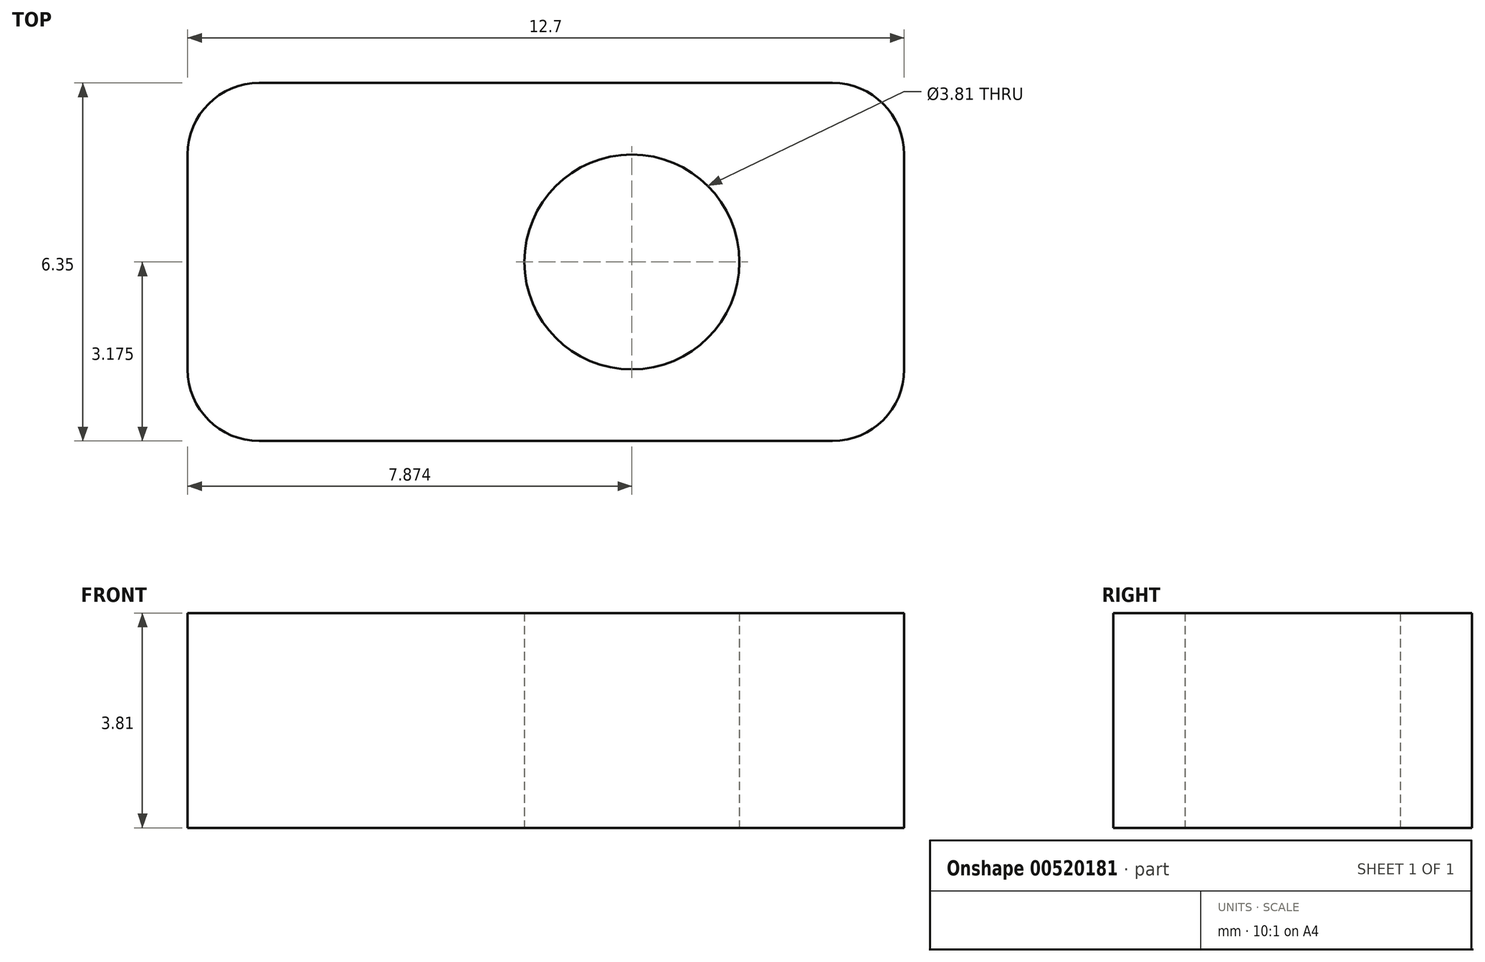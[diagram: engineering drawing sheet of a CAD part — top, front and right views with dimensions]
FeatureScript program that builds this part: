
annotation { "Feature Type Name" : "Feature", "Feature Type Description" : "" }
export const myFeature = defineFeature(function(context is Context, id is Id, definition is map)
    precondition{}
    {
        {
            var Q0;
            Q0=qCreatedBy(makeId("Top.planeOp"),FACE);
            var sketch = newSketch(context, id + "F0", { "sketchPlane" : qUnion([Q0])});
            skLineSegment(sketch, "E0.bottom", {"start": v(0, 0) * mm, "end": v(-12.7, 0) * mm});
            skLineSegment(sketch, "E0.top", {"start": v(0, 6.35) * mm, "end": v(-12.7, 6.35) * mm});
            skLineSegment(sketch, "E0.left", {"start": v(0, 0) * mm, "end": v(0, 6.35) * mm});
            skLineSegment(sketch, "E0.right", {"start": v(-12.7, 0) * mm, "end": v(-12.7, 6.35) * mm});
            skCircle(sketch, "E1", {"center": v(-4.83, 3.17) * mm, "radius": 1.9 * mm});
            skLineSegment(sketch, "E2", {"start": v(-7.21, 3.17) * mm, "end": v(-1.57, 3.17) * mm, "construction": true});
            skLineSegment(sketch, "E3", {"start": v(-4.83, 5.82) * mm, "end": v(-4.83, 0.3) * mm, "construction": true});
            skSolve(sketch);
        }
        {
            var Q0;
            Q0 = qSketchRegion(id + "F0", true);
            extrude(context, id + "F1", {"entities" : qUnion([Q0]), "depth" : 3.8 * mm, "offsetDistance" : 25.4 * mm});
        }
        {
            var Q0;
            Q0=makeQuery(id+"F1.opExtrude","SWEPT_EDGE",EDGE,{"disambiguationData":[OSD([sQuery(id+"F0.wireOp",EDGE,"E0.bottom"),sQuery(id+"F0.wireOp",EDGE,"E0.left")])]});
            var Q1;
            Q1=makeQuery(id+"F1.opExtrude","SWEPT_EDGE",EDGE,{"disambiguationData":[OSD([sQuery(id+"F0.wireOp",EDGE,"E0.top"),sQuery(id+"F0.wireOp",EDGE,"E0.left")])]});
            var Q2;
            Q2=makeQuery(id+"F1.opExtrude","SWEPT_EDGE",EDGE,{"disambiguationData":[OSD([sQuery(id+"F0.wireOp",EDGE,"E0.bottom"),sQuery(id+"F0.wireOp",EDGE,"E0.right")])]});
            var Q3;
            Q3=makeQuery(id+"F1.opExtrude","SWEPT_EDGE",EDGE,{"disambiguationData":[OSD([sQuery(id+"F0.wireOp",EDGE,"E0.top"),sQuery(id+"F0.wireOp",EDGE,"E0.right")])]});
            fillet(context, id + "F2", {"entities" : qUnion([Q0, Q1, Q2, Q3]), "radius" : 1.27 * mm, "tangentPropagation" : true, "allowEdgeOverflow" : false});
        }
    });
